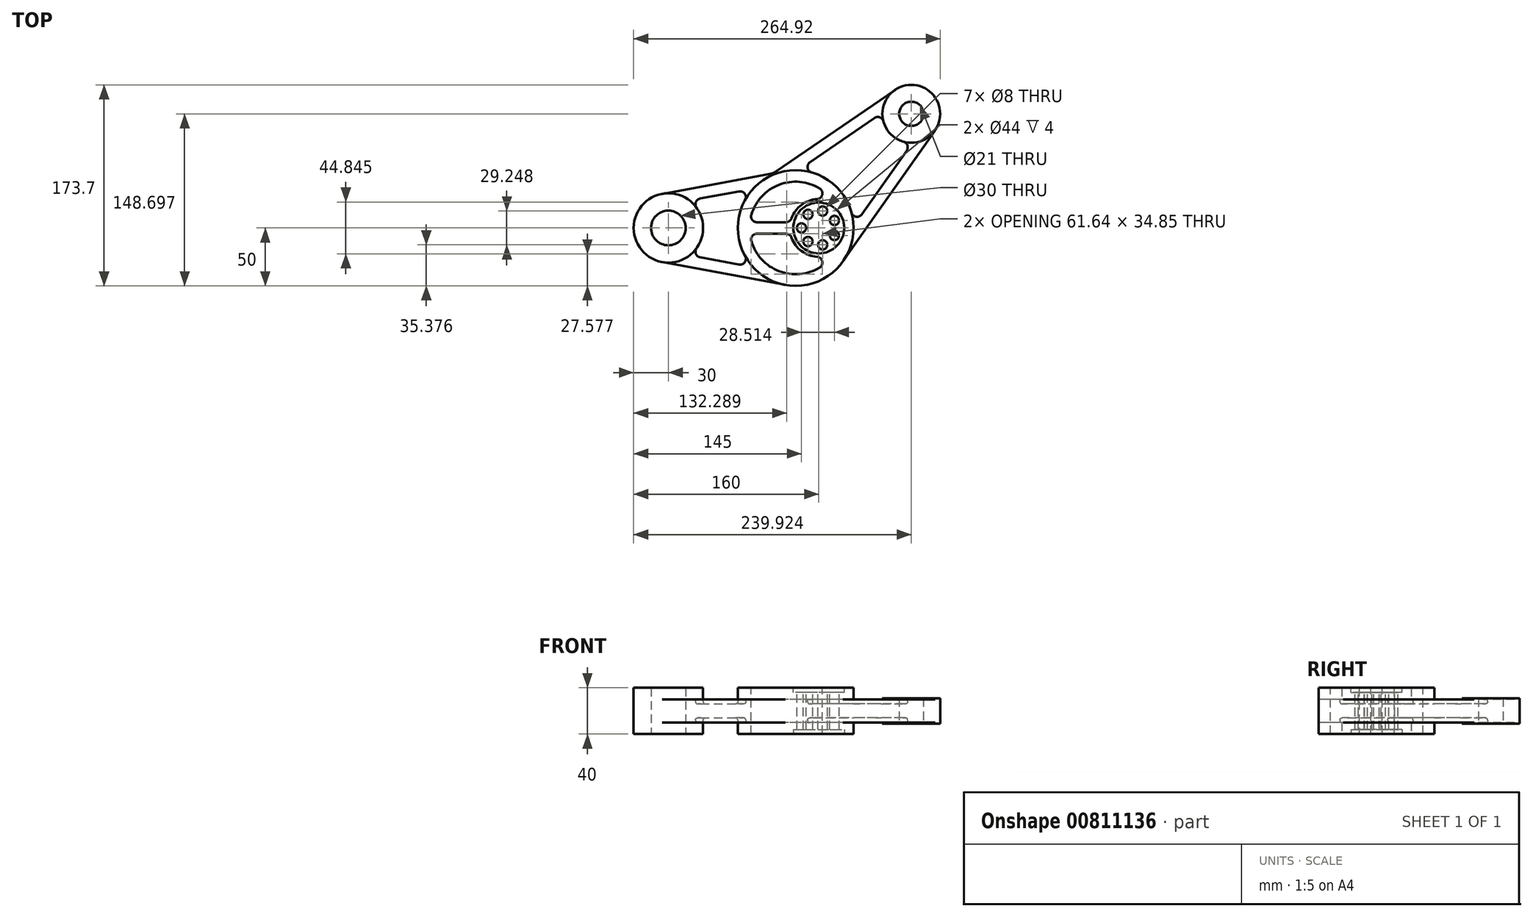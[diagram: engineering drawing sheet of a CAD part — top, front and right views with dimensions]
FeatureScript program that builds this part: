
annotation { "Feature Type Name" : "Feature", "Feature Type Description" : "" }
export const myFeature = defineFeature(function(context is Context, id is Id, definition is map)
    precondition{}
    {
        {
            var Q0;
            Q0=qCreatedBy(makeId("Top.planeOp"),FACE);
            var sketch = newSketch(context, id + "F0", { "sketchPlane" : qUnion([Q0])});
            skCircle(sketch, "E0", {"center": v(-110, 0) * mm, "radius": 15 * mm});
            skCircle(sketch, "E1", {"center": v(-110, 0) * mm, "radius": 30 * mm});
            skCircle(sketch, "E2", {"center": v(0, 0) * mm, "radius": 50 * mm});
            skLineSegment(sketch, "E3", {"start": v(-115.45, 29.5) * mm, "end": v(-9.1, 49.17) * mm});
            skLineSegment(sketch, "E4", {"start": v(-115.45, -29.5) * mm, "end": v(-9.1, -49.17) * mm});
            skLineSegment(sketch, "E5", {"start": v(20, 0) * mm, "end": v(99.92, 98.7) * mm, "construction": true});
            skCircle(sketch, "E6", {"center": v(99.92, 98.7) * mm, "radius": 10.5 * mm});
            skCircle(sketch, "E7", {"center": v(99.92, 98.7) * mm, "radius": 25 * mm});
            skLineSegment(sketch, "E8", {"start": v(120.38, 84.32) * mm, "end": v(40.9, -28.75) * mm});
            skLineSegment(sketch, "E9", {"start": v(85.8, 119.33) * mm, "end": v(-28.24, 41.26) * mm});
            skPoint(sketch, "E10.visualSharp", {"position": v(-19.5, 47.24) * mm});
            skSolve(sketch);
        }
        {
            var Q0;
            Q0 = qSketchRegion(id + "F0", true);
            extrude(context, id + "F1", {"entities" : qUnion([Q0]), "depth" : 40 * mm, "offsetDistance" : 25 * mm});
        }
        {
            var Q0;
            Q0=makeQuery(id+"F1.opExtrude","CAP_FACE",FACE,{"disambiguationData":[OSD([sQuery(id+"F0.wireOp",EDGE,"E0"),sQuery(id+"F0.wireOp",EDGE,"E1"),sQuery(id+"F0.wireOp",EDGE,"E2"),sQuery(id+"F0.wireOp",EDGE,"E3"),sQuery(id+"F0.wireOp",EDGE,"E4"),sQuery(id+"F0.wireOp",EDGE,"E6"),sQuery(id+"F0.wireOp",EDGE,"E7"),sQuery(id+"F0.wireOp",EDGE,"E8"),sQuery(id+"F0.wireOp",EDGE,"E9"),sQuery(id+"F0.wireOp",EDGE,"E10.filletArc")])],"isStart":false});
            var sketch = newSketch(context, id + "F2", { "sketchPlane" : qUnion([Q0])});
            skArc(sketch, "E11", {"start": v(-115.45, -29.5) * mm, "mid": v(-80, 0) * mm, "end": v(-115.45, 29.5) * mm});
            skArc(sketch, "E12", {"start": v(-9.1, -49.17) * mm, "mid": v(18.9, -46.29) * mm, "end": v(40.9, -28.75) * mm});
            skLineSegment(sketch, "E13.0", {"start": v(-115.45, 29.5) * mm, "end": v(-19.5, 47.24) * mm});
            skLineSegment(sketch, "E14.0", {"start": v(-115.45, -29.5) * mm, "end": v(-9.1, -49.17) * mm});
            skArc(sketch, "E15", {"start": v(85.8, 119.33) * mm, "mid": v(82.14, 81.13) * mm, "end": v(120.38, 84.32) * mm});
            skLineSegment(sketch, "E16.0", {"start": v(85.8, 119.33) * mm, "end": v(-19.5, 47.24) * mm});
            skLineSegment(sketch, "E17.0", {"start": v(120.38, 84.32) * mm, "end": v(40.9, -28.75) * mm});
            skCircle(sketch, "E18", {"center": v(0, 0) * mm, "radius": 50 * mm});
            skSolve(sketch);
        }
        {
            var Q0;
            Q0 = qSketchRegion(id + "F2", true);
            extrude(context, id + "F3", {"entities" : qUnion([Q0]), "operationType" : NewBodyOperationType.REMOVE, "oppositeDirection" : true, "depth" : 10 * mm, "offsetDistance" : 25 * mm});
        }
        {
            var Q0;
            Q0=makeQuery(id+"F1.opExtrude","CAP_FACE",FACE,{"disambiguationData":[OSD([sQuery(id+"F0.wireOp",EDGE,"E0"),sQuery(id+"F0.wireOp",EDGE,"E1"),sQuery(id+"F0.wireOp",EDGE,"E2"),sQuery(id+"F0.wireOp",EDGE,"E3"),sQuery(id+"F0.wireOp",EDGE,"E4"),sQuery(id+"F0.wireOp",EDGE,"E6"),sQuery(id+"F0.wireOp",EDGE,"E7"),sQuery(id+"F0.wireOp",EDGE,"E8"),sQuery(id+"F0.wireOp",EDGE,"E9")])],"isStart":true});
            var sketch = newSketch(context, id + "F4", { "sketchPlane" : qUnion([Q0])});
            skArc(sketch, "E19.0", {"start": v(-115.45, 29.5) * mm, "mid": v(-80, 0) * mm, "end": v(-115.45, -29.5) * mm});
            skLineSegment(sketch, "E20.0", {"start": v(-115.45, -29.5) * mm, "end": v(-19.5, -47.24) * mm});
            skLineSegment(sketch, "E21.0", {"start": v(-115.45, 29.5) * mm, "end": v(-9.1, 49.17) * mm});
            skCircle(sketch, "E22.0", {"center": v(0, 0) * mm, "radius": 50 * mm});
            skLineSegment(sketch, "E23.0", {"start": v(85.8, -119.33) * mm, "end": v(-19.5, -47.24) * mm});
            skArc(sketch, "E24.0", {"start": v(85.8, -119.33) * mm, "mid": v(82.14, -81.13) * mm, "end": v(120.38, -84.32) * mm});
            skLineSegment(sketch, "E25.0", {"start": v(120.38, -84.32) * mm, "end": v(40.9, 28.75) * mm});
            skSolve(sketch);
        }
        {
            var Q0;
            Q0 = qSketchRegion(id + "F4", true);
            extrude(context, id + "F5", {"entities" : qUnion([Q0]), "operationType" : NewBodyOperationType.REMOVE, "oppositeDirection" : true, "depth" : 10 * mm, "offsetDistance" : 25 * mm});
        }
        {
            var Q0;
            Q0=makeQuery(id+"F5.boolean.opBoolean","COPY",FACE,{"derivedFrom":makeQuery(id+"F5.opExtrude","CAP_FACE",FACE,{"disambiguationData":[OSD([sQuery(id+"F4.wireOp",EDGE,"E19.0"),sQuery(id+"F4.wireOp",EDGE,"E20.0"),sQuery(id+"F4.wireOp",EDGE,"E21.0"),sQuery(id+"F4.wireOp",EDGE,"E22.0"),sQuery(id+"F4.wireOp",EDGE,"E23.0"),sQuery(id+"F4.wireOp",EDGE,"E24.0"),sQuery(id+"F4.wireOp",EDGE,"E25.0")])],"isStart":false})});
            var sketch = newSketch(context, id + "F6", { "sketchPlane" : qUnion([Q0])});
            skCircle(sketch, "E26.0", {"center": v(0, 0) * mm, "radius": 50 * mm});
            skSolve(sketch);
        }
        {
            var Q0;
            Q0 = qSketchRegion(id + "F6", true);
            extrude(context, id + "F7", {"entities" : qUnion([Q0]), "operationType" : NewBodyOperationType.ADD, "depth" : 10 * mm, "offsetDistance" : 25 * mm});
        }
        {
            var Q0;
            Q0=makeQuery(id+"F3.boolean.opBoolean","COPY",FACE,{"derivedFrom":makeQuery(id+"F3.opExtrude","CAP_FACE",FACE,{"disambiguationData":[OSD([sQuery(id+"F2.wireOp",EDGE,"E11"),sQuery(id+"F2.wireOp",EDGE,"E13.0"),sQuery(id+"F2.wireOp",EDGE,"E14.0"),sQuery(id+"F2.wireOp",EDGE,"E15"),sQuery(id+"F2.wireOp",EDGE,"E16.0"),sQuery(id+"F2.wireOp",EDGE,"E17.0"),sQuery(id+"F2.wireOp",EDGE,"E18")])],"isStart":false})});
            var sketch = newSketch(context, id + "F8", { "sketchPlane" : qUnion([Q0])});
            skCircle(sketch, "E27.0", {"center": v(0, 0) * mm, "radius": 50 * mm});
            skSolve(sketch);
        }
        {
            var Q0;
            Q0 = qSketchRegion(id + "F8", true);
            extrude(context, id + "F9", {"entities" : qUnion([Q0]), "operationType" : NewBodyOperationType.ADD, "depth" : 10 * mm, "offsetDistance" : 25 * mm});
        }
        {
            var Q0;
            Q0=makeQuery(id+"F2.imprint","IMPRINT",FACE,{"disambiguationData":[TD([[makeQuery(id+"F2.imprint","IMPRINT",EDGE,{"derivedFrom":sQuery(id+"F2.wireOp",EDGE,"E15")}),1.0]])]});
            var sketch = newSketch(context, id + "F10", { "sketchPlane" : qUnion([Q0])});
            skCircle(sketch, "E28.0", {"center": v(99.92, 98.7) * mm, "radius": 25 * mm});
            skSolve(sketch);
        }
        {
            var Q0;
            Q0 = qSketchRegion(id + "F10", true);
            extrude(context, id + "F11", {"entities" : qUnion([Q0]), "operationType" : NewBodyOperationType.REMOVE, "oppositeDirection" : true, "depth" : 9 * mm, "offsetDistance" : 25 * mm});
        }
        {
            var Q0;
            {var subQ0=sQuery(id+"F0.wireOp",EDGE,"E6");var subQ1=sQuery(id+"F0.wireOp",EDGE,"E7");Q0=makeQuery(id+"F5.boolean.opBoolean","SPLIT",FACE,{"disambiguationData":[TD([makeQuery(id+"F1.opExtrude","SWEPT_FACE",FACE,{"disambiguationData":[OSD([subQ0])]})])],"derivedFrom":makeQuery(id+"F1.opExtrude","CAP_FACE",FACE,{"disambiguationData":[OSD([sQuery(id+"F0.wireOp",EDGE,"E0"),sQuery(id+"F0.wireOp",EDGE,"E1"),sQuery(id+"F0.wireOp",EDGE,"E2"),sQuery(id+"F0.wireOp",EDGE,"E3"),sQuery(id+"F0.wireOp",EDGE,"E4"),subQ0,subQ1,sQuery(id+"F0.wireOp",EDGE,"E8"),sQuery(id+"F0.wireOp",EDGE,"E9")])],"isStart":true})});}
            var sketch = newSketch(context, id + "F12", { "sketchPlane" : qUnion([Q0])});
            skCircle(sketch, "E29.0", {"center": v(99.92, -98.7) * mm, "radius": 25 * mm});
            skSolve(sketch);
        }
        {
            var Q0;
            Q0 = qSketchRegion(id + "F12", true);
            extrude(context, id + "F13", {"entities" : qUnion([Q0]), "operationType" : NewBodyOperationType.REMOVE, "oppositeDirection" : true, "depth" : 9 * mm, "offsetDistance" : 25 * mm});
        }
        {
            var Q0;
            {var subQ0=sQuery(id+"F2.wireOp",EDGE,"E18");var subQ1=makeQuery(id+"F2.imprint","INTERSECT",VERTEX,{"derivedFrom":[sQuery(id+"F2.wireOp",EDGE,"E14.0"),subQ0]});Q0=makeQuery(id+"F2.imprint","IMPRINT",FACE,{"disambiguationData":[TD([[makeQuery(id+"F2.imprint","IMPRINT",EDGE,{"disambiguationData":[TD([[subQ1,-1.0]])],"derivedFrom":subQ0}),1.0]])]});}
            var sketch = newSketch(context, id + "F14", { "sketchPlane" : qUnion([Q0])});
            skCircle(sketch, "E30", {"center": v(20, 0) * mm, "radius": 22 * mm});
            skSolve(sketch);
        }
        {
            var Q0;
            Q0 = qSketchRegion(id + "F14", true);
            extrude(context, id + "F15", {"entities" : qUnion([Q0]), "operationType" : NewBodyOperationType.REMOVE, "oppositeDirection" : true, "depth" : 4 * mm, "offsetDistance" : 25 * mm});
        }
        {
            var Q0;
            Q0=makeQuery(id+"F7.opExtrude","CAP_FACE",FACE,{"disambiguationData":[OSD([sQuery(id+"F6.wireOp",EDGE,"E26.0")])],"isStart":false});
            var sketch = newSketch(context, id + "F16", { "sketchPlane" : qUnion([Q0])});
            skCircle(sketch, "E31.0", {"center": v(20, 0) * mm, "radius": 22 * mm});
            skSolve(sketch);
        }
        {
            var Q0;
            Q0 = qSketchRegion(id + "F16", true);
            extrude(context, id + "F17", {"entities" : qUnion([Q0]), "operationType" : NewBodyOperationType.REMOVE, "oppositeDirection" : true, "depth" : 4 * mm, "offsetDistance" : 25 * mm});
        }
        {
            var Q0;
            {var subQ0=sQuery(id+"F2.wireOp",EDGE,"E18");var subQ1=makeQuery(id+"F2.imprint","INTERSECT",VERTEX,{"derivedFrom":[sQuery(id+"F2.wireOp",EDGE,"E14.0"),subQ0]});Q0=makeQuery(id+"F2.imprint","IMPRINT",FACE,{"disambiguationData":[TD([[makeQuery(id+"F2.imprint","IMPRINT",EDGE,{"disambiguationData":[TD([[subQ1,-1.0]])],"derivedFrom":subQ0}),1.0]])]});}
            var sketch = newSketch(context, id + "F18", { "sketchPlane" : qUnion([Q0])});
            skCircle(sketch, "E32.0", {"center": v(20, 0) * mm, "radius": 22 * mm, "construction": true});
            skCircle(sketch, "E33", {"center": v(20, 0) * mm, "radius": 15 * mm, "construction": true});
            skCircle(sketch, "E34", {"center": v(5, 0) * mm, "radius": 4 * mm});
            skCircle(sketch, "E35.1.0", {"center": v(10.65, -11.73) * mm, "radius": 4 * mm});
            skCircle(sketch, "E35.2.0", {"center": v(23.34, -14.62) * mm, "radius": 4 * mm});
            skCircle(sketch, "E35.3.0", {"center": v(33.51, -6.5) * mm, "radius": 4 * mm});
            skCircle(sketch, "E35.4.0", {"center": v(33.51, 6.5) * mm, "radius": 4 * mm});
            skCircle(sketch, "E35.5.0", {"center": v(23.34, 14.62) * mm, "radius": 4 * mm});
            skCircle(sketch, "E35.6.0", {"center": v(10.65, 11.73) * mm, "radius": 4 * mm});
            skArc(sketch, "E36", {"start": v(18.44, 24.95) * mm, "mid": v(4.94, 19.95) * mm, "end": v(-3.57, 8.33) * mm});
            skArc(sketch, "E37", {"start": v(-38.33, -11.43) * mm, "mid": v(-14.4, -37.32) * mm, "end": v(20.71, -34.22) * mm});
            skLineSegment(sketch, "E38", {"start": v(-33.54, 5) * mm, "end": v(-8.28, 5) * mm});
            skLineSegment(sketch, "E39", {"start": v(-33.54, -5) * mm, "end": v(-8.28, -5) * mm});
            skPoint(sketch, "E40.visualSharp", {"position": v(-39.69, 5) * mm});
            skArc(sketch, "E40.filletArc", {"start": v(-38.33, 11.43) * mm, "mid": v(-37.55, 7.01) * mm, "end": v(-33.54, 5) * mm});
            skPoint(sketch, "E41.visualSharp", {"position": v(-39.69, -5) * mm});
            skArc(sketch, "E41.filletArc", {"start": v(-33.54, -5) * mm, "mid": v(-37.55, -7.01) * mm, "end": v(-38.33, -11.43) * mm});
            skArc(sketch, "E42.trimOffspring", {"start": v(20.71, 34.22) * mm, "mid": v(-14.4, 37.32) * mm, "end": v(-38.33, 11.43) * mm});
            skArc(sketch, "E43.trimOffspring", {"start": v(-3.57, -8.33) * mm, "mid": v(4.94, -19.95) * mm, "end": v(18.44, -24.95) * mm});
            skPoint(sketch, "E44.visualSharp", {"position": v(-4.5, 5) * mm});
            skArc(sketch, "E44.filletArc", {"start": v(-8.28, 5) * mm, "mid": v(-5.4, 5.92) * mm, "end": v(-3.57, 8.33) * mm});
            skPoint(sketch, "E45.visualSharp", {"position": v(-4.5, -5) * mm});
            skArc(sketch, "E45.filletArc", {"start": v(-3.57, -8.33) * mm, "mid": v(-5.4, -5.92) * mm, "end": v(-8.28, -5) * mm});
            skArc(sketch, "E46", {"start": v(18.44, 24.95) * mm, "mid": v(22.98, 28.75) * mm, "end": v(20.71, 34.22) * mm});
            skArc(sketch, "E47", {"start": v(20.71, -34.22) * mm, "mid": v(22.98, -28.75) * mm, "end": v(18.44, -24.95) * mm});
            skArc(sketch, "E48.0", {"start": v(-85.68, -17.57) * mm, "mid": v(-80, 0) * mm, "end": v(-85.68, 17.57) * mm, "construction": true});
            skArc(sketch, "E49.0", {"start": v(75.77, 92.26) * mm, "mid": v(82.14, 81.13) * mm, "end": v(93.19, 74.62) * mm, "construction": true});
            skLineSegment(sketch, "E50.0", {"start": v(-115.45, 29.5) * mm, "end": v(-19.5, 47.24) * mm, "construction": true});
            skLineSegment(sketch, "E51.0", {"start": v(-115.45, -29.5) * mm, "end": v(-9.1, -49.17) * mm, "construction": true});
            skLineSegment(sketch, "E52.0", {"start": v(120.38, 84.32) * mm, "end": v(40.9, -28.75) * mm, "construction": true});
            skLineSegment(sketch, "E53.0", {"start": v(85.8, 119.33) * mm, "end": v(-19.5, 47.24) * mm, "construction": true});
            skLineSegment(sketch, "E54.0", {"start": v(-82.54, 25.42) * mm, "end": v(-49, 31.62) * mm, "construction": true});
            skLineSegment(sketch, "E55.0", {"start": v(-82.54, -25.42) * mm, "end": v(-49, -31.62) * mm, "construction": true});
            skLineSegment(sketch, "E56.0", {"start": v(68.11, 95.1) * mm, "end": v(12.41, 56.97) * mm, "construction": true});
            skLineSegment(sketch, "E57.0", {"start": v(95.93, 66.93) * mm, "end": v(57.12, 11.71) * mm, "construction": true});
            skArc(sketch, "E58", {"start": v(-82.54, 25.42) * mm, "mid": v(-86.27, 22.36) * mm, "end": v(-85.68, 17.57) * mm, "construction": true});
            skArc(sketch, "E59", {"start": v(-43.71, 24.28) * mm, "mid": v(-44.02, 29.62) * mm, "end": v(-49, 31.62) * mm, "construction": true});
            skArc(sketch, "E60", {"start": v(-85.68, -17.57) * mm, "mid": v(-86.27, -22.36) * mm, "end": v(-82.54, -25.42) * mm, "construction": true});
            skArc(sketch, "E61", {"start": v(-49, -31.62) * mm, "mid": v(-44.02, -29.62) * mm, "end": v(-43.71, -24.28) * mm, "construction": true});
            skPoint(sketch, "E62.orphan", {"position": v(-115.45, 29.5) * mm});
            skPoint(sketch, "E63.orphan", {"position": v(-115.45, -29.5) * mm});
            skArc(sketch, "E64.trimOffspring", {"start": v(-43.71, 24.28) * mm, "mid": v(-50, 0) * mm, "end": v(-43.71, -24.28) * mm, "construction": true});
            skPoint(sketch, "E65.orphan", {"position": v(85.8, 119.33) * mm});
            skPoint(sketch, "E66.orphan", {"position": v(120.38, 84.32) * mm});
            skArc(sketch, "E67.trimOffspring", {"start": v(48.2, 13.26) * mm, "mid": v(35.57, 35.14) * mm, "end": v(13.85, 48.04) * mm, "construction": true});
            skArc(sketch, "E68", {"start": v(12.41, 56.97) * mm, "mid": v(10.3, 52.05) * mm, "end": v(13.85, 48.04) * mm, "construction": true});
            skArc(sketch, "E69", {"start": v(75.77, 92.26) * mm, "mid": v(72.67, 95.66) * mm, "end": v(68.11, 95.1) * mm, "construction": true});
            skArc(sketch, "E70", {"start": v(95.93, 66.93) * mm, "mid": v(96.55, 71.49) * mm, "end": v(93.19, 74.62) * mm, "construction": true});
            skArc(sketch, "E71", {"start": v(48.2, 13.26) * mm, "mid": v(52.17, 9.66) * mm, "end": v(57.12, 11.71) * mm, "construction": true});
            skSolve(sketch);
        }
        {
            var Q0;
            Q0 = qSketchRegion(id + "F18", true);
            extrude(context, id + "F19", {"entities" : qUnion([Q0]), "operationType" : NewBodyOperationType.REMOVE, "oppositeDirection" : true, "depth" : 40 * mm, "offsetDistance" : 25 * mm});
        }
        {
            var Q0;
            Q0=makeQuery(id+"F2.imprint","IMPRINT",FACE,{"disambiguationData":[TD([[makeQuery(id+"F2.imprint","IMPRINT",EDGE,{"derivedFrom":sQuery(id+"F2.wireOp",EDGE,"E11")}),1.0]])]});
            var sketch = newSketch(context, id + "F20", { "sketchPlane" : qUnion([Q0])});
            skLineSegment(sketch, "E72.0", {"start": v(-82.54, 25.42) * mm, "end": v(-49, 31.62) * mm});
            skArc(sketch, "E73.0", {"start": v(-82.54, 25.42) * mm, "mid": v(-86.27, 22.36) * mm, "end": v(-85.68, 17.57) * mm});
            skArc(sketch, "E74.0", {"start": v(-43.71, 24.28) * mm, "mid": v(-44.02, 29.62) * mm, "end": v(-49, 31.62) * mm});
            skArc(sketch, "E75.0", {"start": v(-49, -31.62) * mm, "mid": v(-44.02, -29.62) * mm, "end": v(-43.71, -24.28) * mm});
            skLineSegment(sketch, "E76.0", {"start": v(-82.54, -25.42) * mm, "end": v(-49, -31.62) * mm});
            skArc(sketch, "E77.0", {"start": v(-85.68, -17.57) * mm, "mid": v(-86.27, -22.36) * mm, "end": v(-82.54, -25.42) * mm});
            skLineSegment(sketch, "E78.0", {"start": v(68.11, 95.1) * mm, "end": v(12.41, 56.97) * mm});
            skLineSegment(sketch, "E79.0", {"start": v(95.93, 66.93) * mm, "end": v(57.12, 11.71) * mm});
            skArc(sketch, "E80.0", {"start": v(95.93, 66.93) * mm, "mid": v(96.55, 71.49) * mm, "end": v(93.19, 74.62) * mm});
            skArc(sketch, "E81.0", {"start": v(75.77, 92.26) * mm, "mid": v(72.67, 95.66) * mm, "end": v(68.11, 95.1) * mm});
            skArc(sketch, "E82.0", {"start": v(48.2, 13.26) * mm, "mid": v(52.17, 9.66) * mm, "end": v(57.12, 11.71) * mm});
            skArc(sketch, "E83.0", {"start": v(12.41, 56.97) * mm, "mid": v(10.3, 52.05) * mm, "end": v(13.85, 48.04) * mm});
            skArc(sketch, "E84.0", {"start": v(-85.68, -17.57) * mm, "mid": v(-80, 0) * mm, "end": v(-85.68, 17.57) * mm});
            skArc(sketch, "E85.0", {"start": v(48.2, 13.26) * mm, "mid": v(35.57, 35.14) * mm, "end": v(13.85, 48.04) * mm});
            skArc(sketch, "E86.0.1", {"start": v(-43.71, -24.28) * mm, "mid": v(-50, 0) * mm, "end": v(-43.71, 24.28) * mm});
            skArc(sketch, "E86.0.3", {"start": v(93.19, 74.62) * mm, "mid": v(82.14, 81.13) * mm, "end": v(75.77, 92.26) * mm});
            skArc(sketch, "E86.0.6", {"start": v(-85.68, 17.57) * mm, "mid": v(-80, 0) * mm, "end": v(-85.68, -17.57) * mm});
            skPoint(sketch, "E87.orphan", {"position": v(-115.45, 29.5) * mm});
            skArc(sketch, "E88.trimOffspring", {"start": v(13.85, 48.04) * mm, "mid": v(35.57, 35.14) * mm, "end": v(48.2, 13.26) * mm});
            skPoint(sketch, "E89.0.2.end.orphan", {"position": v(120.38, 84.32) * mm});
            skPoint(sketch, "E90.orphan", {"position": v(-115.45, -29.5) * mm});
            skArc(sketch, "E91.trimOffspring", {"start": v(-43.71, 24.28) * mm, "mid": v(-50, 0) * mm, "end": v(-43.71, -24.28) * mm});
            skPoint(sketch, "E89.0.4.end.orphan", {"position": v(-19.5, 47.24) * mm});
            skPoint(sketch, "E89.0.4.start.orphan", {"position": v(85.8, 119.33) * mm});
            skPoint(sketch, "E92.orphan", {"position": v(40.9, -28.75) * mm});
            skSolve(sketch);
        }
        {
            var Q0;
            Q0 = qSketchRegion(id + "F20", true);
            extrude(context, id + "F21", {"entities" : qUnion([Q0]), "operationType" : NewBodyOperationType.REMOVE, "oppositeDirection" : true, "depth" : 14 * mm, "offsetDistance" : 25 * mm});
        }
        {
            var Q0;
            {var subQ0=sQuery(id+"F0.wireOp",EDGE,"E0");var subQ1=sQuery(id+"F0.wireOp",EDGE,"E1");Q0=makeQuery(id+"F5.boolean.opBoolean","SPLIT",FACE,{"disambiguationData":[TD([makeQuery(id+"F1.opExtrude","SWEPT_FACE",FACE,{"disambiguationData":[OSD([subQ0])]})])],"derivedFrom":makeQuery(id+"F1.opExtrude","CAP_FACE",FACE,{"disambiguationData":[OSD([subQ0,subQ1,sQuery(id+"F0.wireOp",EDGE,"E2"),sQuery(id+"F0.wireOp",EDGE,"E3"),sQuery(id+"F0.wireOp",EDGE,"E4"),sQuery(id+"F0.wireOp",EDGE,"E6"),sQuery(id+"F0.wireOp",EDGE,"E7"),sQuery(id+"F0.wireOp",EDGE,"E8"),sQuery(id+"F0.wireOp",EDGE,"E9")])],"isStart":true})});}
            var sketch = newSketch(context, id + "F22", { "sketchPlane" : qUnion([Q0])});
            skLineSegment(sketch, "E93.0", {"start": v(-82.54, 25.42) * mm, "end": v(-49, 31.62) * mm});
            skArc(sketch, "E94.0", {"start": v(-49, 31.62) * mm, "mid": v(-44.02, 29.62) * mm, "end": v(-43.71, 24.28) * mm});
            skLineSegment(sketch, "E95.0", {"start": v(-82.54, -25.42) * mm, "end": v(-49, -31.62) * mm});
            skArc(sketch, "E96.0", {"start": v(-43.71, -24.28) * mm, "mid": v(-44.02, -29.62) * mm, "end": v(-49, -31.62) * mm});
            skArc(sketch, "E97.0", {"start": v(-82.54, -25.42) * mm, "mid": v(-86.27, -22.36) * mm, "end": v(-85.68, -17.57) * mm});
            skArc(sketch, "E98.0", {"start": v(-85.68, 17.57) * mm, "mid": v(-86.27, 22.36) * mm, "end": v(-82.54, 25.42) * mm});
            skArc(sketch, "E99.0", {"start": v(-85.68, 17.57) * mm, "mid": v(-80, 0) * mm, "end": v(-85.68, -17.57) * mm});
            skArc(sketch, "E100.0", {"start": v(-43.71, -24.28) * mm, "mid": v(-50, 0) * mm, "end": v(-43.71, 24.28) * mm});
            skArc(sketch, "E101.0", {"start": v(95.93, -66.93) * mm, "mid": v(96.55, -71.49) * mm, "end": v(93.19, -74.62) * mm});
            skLineSegment(sketch, "E102.0", {"start": v(95.93, -66.93) * mm, "end": v(57.12, -11.71) * mm});
            skArc(sketch, "E103.0", {"start": v(48.2, -13.26) * mm, "mid": v(52.17, -9.66) * mm, "end": v(57.12, -11.71) * mm});
            skArc(sketch, "E104.0", {"start": v(13.85, -48.04) * mm, "mid": v(35.57, -35.14) * mm, "end": v(48.2, -13.26) * mm});
            skArc(sketch, "E105.0", {"start": v(12.41, -56.97) * mm, "mid": v(10.3, -52.05) * mm, "end": v(13.85, -48.04) * mm});
            skLineSegment(sketch, "E106.0", {"start": v(68.11, -95.1) * mm, "end": v(12.41, -56.97) * mm});
            skArc(sketch, "E107.0", {"start": v(75.77, -92.26) * mm, "mid": v(72.67, -95.66) * mm, "end": v(68.11, -95.1) * mm});
            skArc(sketch, "E108.0", {"start": v(75.77, -92.26) * mm, "mid": v(82.14, -81.13) * mm, "end": v(93.19, -74.62) * mm});
            skPoint(sketch, "E109.orphan", {"position": v(-115.45, 29.5) * mm});
            skPoint(sketch, "E110.orphan", {"position": v(-115.45, -29.5) * mm});
            skPoint(sketch, "E111.orphan", {"position": v(85.8, -119.33) * mm});
            skPoint(sketch, "E112.orphan", {"position": v(120.38, -84.32) * mm});
            skSolve(sketch);
        }
        {
            var Q0;
            Q0 = qSketchRegion(id + "F22", true);
            extrude(context, id + "F23", {"entities" : qUnion([Q0]), "operationType" : NewBodyOperationType.REMOVE, "oppositeDirection" : true, "depth" : 14 * mm, "offsetDistance" : 25 * mm});
        }
        {
            var Q0;
            Q0=makeQuery(id+"F21.boolean.opBoolean","COPY",FACE,{"derivedFrom":makeQuery(id+"F21.opExtrude","CAP_FACE",FACE,{"disambiguationData":[OSD([sQuery(id+"F20.wireOp",EDGE,"E72.0"),sQuery(id+"F20.wireOp",EDGE,"E73.0"),sQuery(id+"F20.wireOp",EDGE,"E74.0"),sQuery(id+"F20.wireOp",EDGE,"E75.0"),sQuery(id+"F20.wireOp",EDGE,"E76.0"),sQuery(id+"F20.wireOp",EDGE,"E77.0"),sQuery(id+"F20.wireOp",EDGE,"E86.0.6"),sQuery(id+"F20.wireOp",EDGE,"E91.trimOffspring")])],"isStart":false})});
            var Q1;
            Q1=makeQuery(id+"F21.boolean.opBoolean","COPY",FACE,{"derivedFrom":makeQuery(id+"F21.opExtrude","CAP_FACE",FACE,{"disambiguationData":[OSD([sQuery(id+"F20.wireOp",EDGE,"E78.0"),sQuery(id+"F20.wireOp",EDGE,"E79.0"),sQuery(id+"F20.wireOp",EDGE,"E80.0"),sQuery(id+"F20.wireOp",EDGE,"E81.0"),sQuery(id+"F20.wireOp",EDGE,"E82.0"),sQuery(id+"F20.wireOp",EDGE,"E83.0"),sQuery(id+"F20.wireOp",EDGE,"E86.0.3"),sQuery(id+"F20.wireOp",EDGE,"E88.trimOffspring")])],"isStart":false})});
            fillet(context, id + "F24", {"entities" : qUnion([Q0, Q1]), "radius" : 2 * mm, "tangentPropagation" : true, "allowEdgeOverflow" : false});
        }
        {
            var Q0;
            Q0=makeQuery(id+"F23.boolean.opBoolean","COPY",FACE,{"derivedFrom":makeQuery(id+"F23.opExtrude","CAP_FACE",FACE,{"disambiguationData":[OSD([sQuery(id+"F22.wireOp",EDGE,"E101.0"),sQuery(id+"F22.wireOp",EDGE,"E102.0"),sQuery(id+"F22.wireOp",EDGE,"E103.0"),sQuery(id+"F22.wireOp",EDGE,"E104.0"),sQuery(id+"F22.wireOp",EDGE,"E105.0"),sQuery(id+"F22.wireOp",EDGE,"E106.0"),sQuery(id+"F22.wireOp",EDGE,"E107.0"),sQuery(id+"F22.wireOp",EDGE,"E108.0")])],"isStart":false})});
            var Q1;
            Q1=makeQuery(id+"F23.boolean.opBoolean","COPY",FACE,{"derivedFrom":makeQuery(id+"F23.opExtrude","CAP_FACE",FACE,{"disambiguationData":[OSD([sQuery(id+"F22.wireOp",EDGE,"E93.0"),sQuery(id+"F22.wireOp",EDGE,"E94.0"),sQuery(id+"F22.wireOp",EDGE,"E95.0"),sQuery(id+"F22.wireOp",EDGE,"E96.0"),sQuery(id+"F22.wireOp",EDGE,"E97.0"),sQuery(id+"F22.wireOp",EDGE,"E98.0"),sQuery(id+"F22.wireOp",EDGE,"E99.0"),sQuery(id+"F22.wireOp",EDGE,"E100.0")])],"isStart":false})});
            fillet(context, id + "F25", {"entities" : qUnion([Q0, Q1]), "radius" : 2 * mm, "tangentPropagation" : true, "allowEdgeOverflow" : false});
        }
        {
            var Q0;
            Q0=makeQuery(id+"F1.opExtrude","SWEPT_EDGE",EDGE,{"disambiguationData":[OSD([sQuery(id+"F0.wireOp",EDGE,"E3"),sQuery(id+"F0.wireOp",EDGE,"E9")])]});
            fillet(context, id + "F26", {"entities" : qUnion([Q0]), "radius" : 12 * mm, "tangentPropagation" : true, "allowEdgeOverflow" : false});
        }
    });
